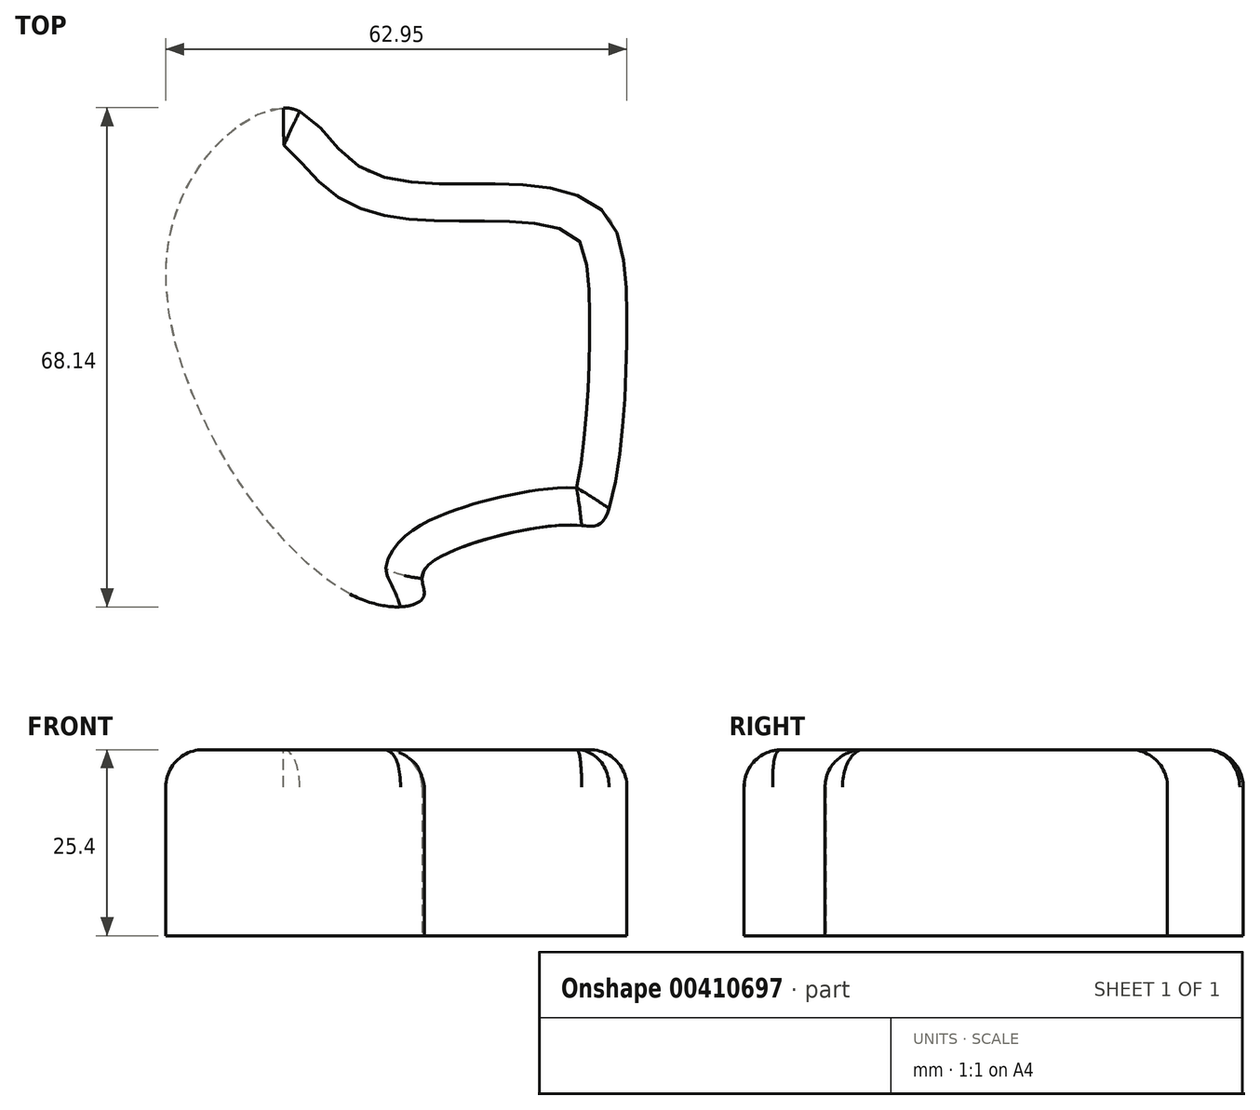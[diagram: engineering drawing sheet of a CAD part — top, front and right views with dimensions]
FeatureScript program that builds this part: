
annotation { "Feature Type Name" : "Feature", "Feature Type Description" : "" }
export const myFeature = defineFeature(function(context is Context, id is Id, definition is map)
    precondition{}
    {
        {
            var Q0;
            Q0=qCreatedBy(makeId("Top.planeOp"),FACE);
            var sketch = newSketch(context, id + "F0", { "sketchPlane" : qUnion([Q0])});
            skFitSpline(sketch, "E0", {"points": [v(-10.1, -39.83) * mm, v(-35.06, 7.07) * mm, v(-18.45, 26.52) * mm, v(-8.95, 18.62) * mm, v(10.06, 16.2) * mm, v(23.93, 12.93) * mm, v(27.67, 0) * mm, v(24.57, -29.68) * mm, v(19.7, -30.39) * mm, v(0, -36.6) * mm, v(0, -40.1) * mm, v(-10.1, -39.83) * mm]});
            skSolve(sketch);
        }
        {
            var Q0;
            Q0=makeQuery(id+"F0.imprint","IMPRINT",FACE,{"disambiguationData":[TD([[makeQuery(id+"F0.imprint","IMPRINT",EDGE,{"derivedFrom":sQuery(id+"F0.wireOp",EDGE,"E0")}),-1.0]])]});
            extrude(context, id + "F1", {"entities" : qUnion([Q0]), "depth" : 25.4 * mm});
        }
        {
            var Q0;
            Q0=makeQuery(id+"F1.opExtrude","CAP_EDGE",EDGE,{"disambiguationData":[OSD([sQuery(id+"F0.wireOp",EDGE,"E0")])],"isStart":false});
            fillet(context, id + "F2", {"entities" : qUnion([Q0]), "radius" : 5.08 * mm, "allowEdgeOverflow" : false});
        }
    });
